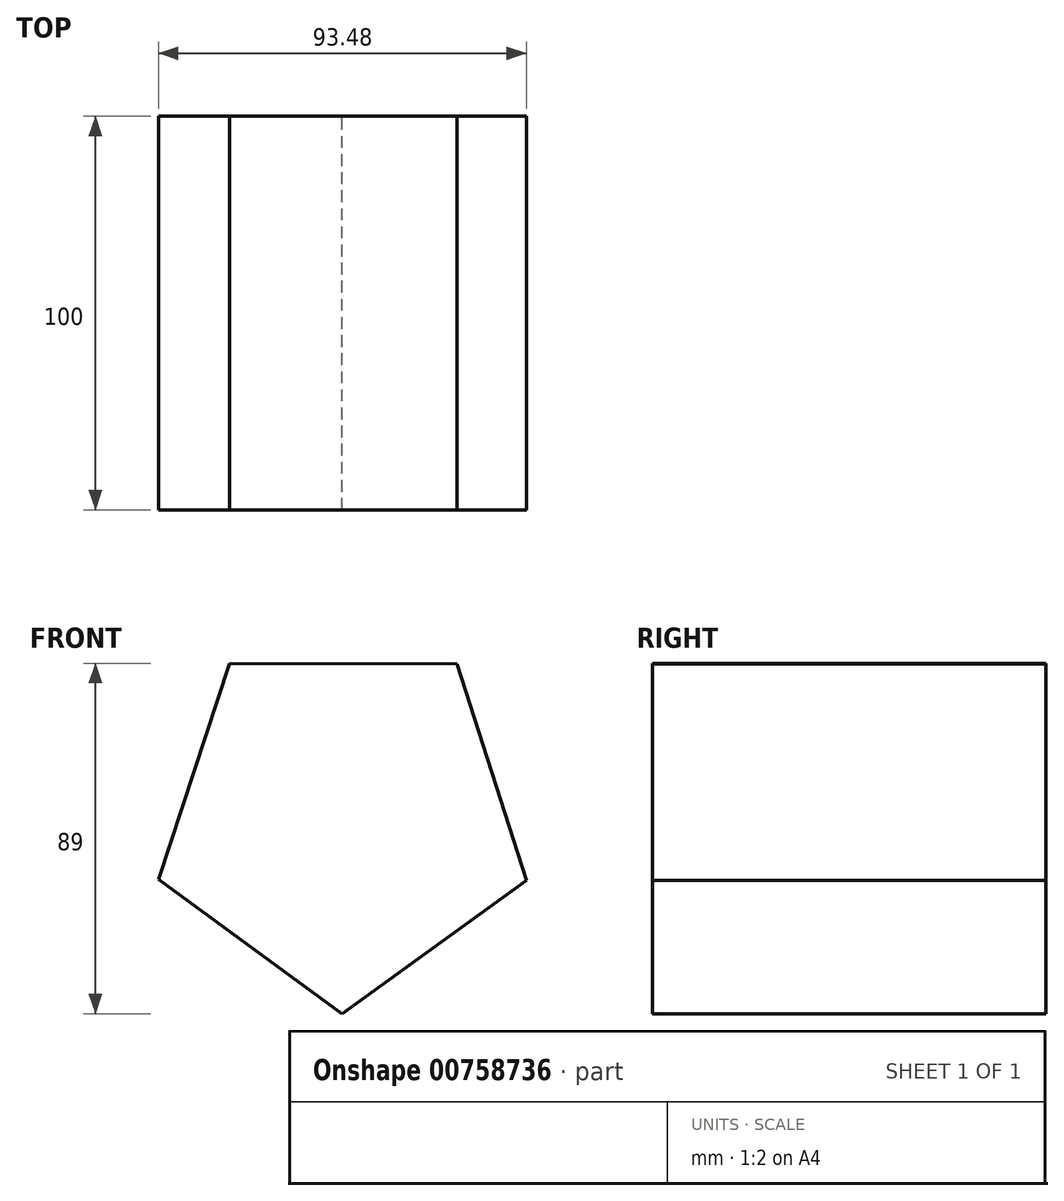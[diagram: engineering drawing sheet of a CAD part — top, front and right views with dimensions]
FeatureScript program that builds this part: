
annotation { "Feature Type Name" : "Feature", "Feature Type Description" : "" }
export const myFeature = defineFeature(function(context is Context, id is Id, definition is map)
    precondition{}
    {
        {
            var Q0;
            Q0=qCreatedBy(makeId("Front.planeOp"),FACE);
            var sketch = newSketch(context, id + "F0", { "sketchPlane" : qUnion([Q0])});
            skCircle(sketch, "E0.cCircle", {"center": v(0, 0) * mm, "radius": 39.76 * mm, "construction": true});
            skLineSegment(sketch, "E0.0", {"start": v(-46.79, -15.04) * mm, "end": v(-28.76, 39.85) * mm});
            skLineSegment(sketch, "E0.1", {"start": v(-28.76, 39.85) * mm, "end": v(29.01, 39.67) * mm});
            skLineSegment(sketch, "E0.2", {"start": v(29.01, 39.67) * mm, "end": v(46.7, -15.33) * mm});
            skLineSegment(sketch, "E0.3", {"start": v(46.7, -15.33) * mm, "end": v(-0.16, -49.15) * mm});
            skLineSegment(sketch, "E0.4", {"start": v(-0.16, -49.15) * mm, "end": v(-46.79, -15.04) * mm});
            skPoint(sketch, "E0.0.midPoint", {"position": v(-37.77, 12.4) * mm});
            skSolve(sketch);
        }
        {
            var Q0;
            Q0=makeQuery(id+"F0.imprint","IMPRINT",FACE,{"disambiguationData":[TD([[makeQuery(id+"F0.imprint","IMPRINT",EDGE,{"derivedFrom":sQuery(id+"F0.wireOp",EDGE,"E0.0")}),-1.0]])]});
            extrude(context, id + "F1", {"entities" : qUnion([Q0]), "depth" : 100 * mm, "offsetDistance" : 25.4 * mm});
        }
    });
